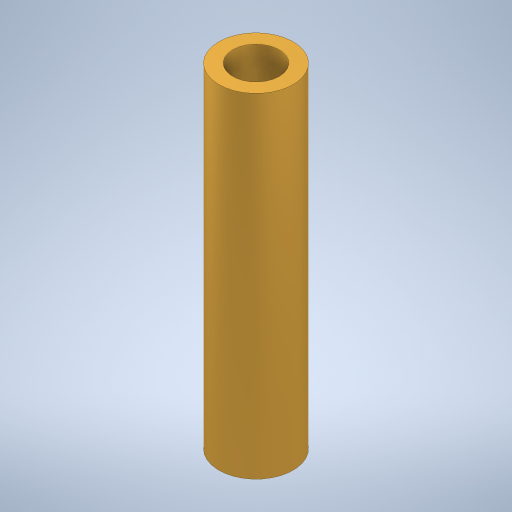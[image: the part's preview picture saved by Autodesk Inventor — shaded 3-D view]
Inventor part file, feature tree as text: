
AUTODESK INVENTOR PART (.ipt)
format: ipt  version: 2023 (Build 270158000, 158)  size: 245,248 bytes
history: native  units: mm
features: other x1, extrude x1, hole x1, sketch x1
ambient origin geometry x8: Origin, YZ Plane, XZ Plane, XY Plane, X Axis, Y Axis, Z Axis, Center Point
bodies: Body1 (feature_tree)
feature tree (4):
  other  "Sólido1"
  extrude  "Extrusão1"  Depth=36.0mm TaperAngle=0.0deg
  hole  "Furo1"  [1 undecoded]
  sketch  "Esboço2"  dims[d1=8.0mm d2=36.0mm d3=0.0mm d4=5.0mm d5=10.0mm d6=4.0mm d7=2.0mm d8=90.0deg d9=0.5mm d10=20.594885mm]
note: 1 required parameter value undecoded (feature->parameter linkage not recoverable at this tier; creation-order binding heuristic only, values carry confidence <= 0.55)
